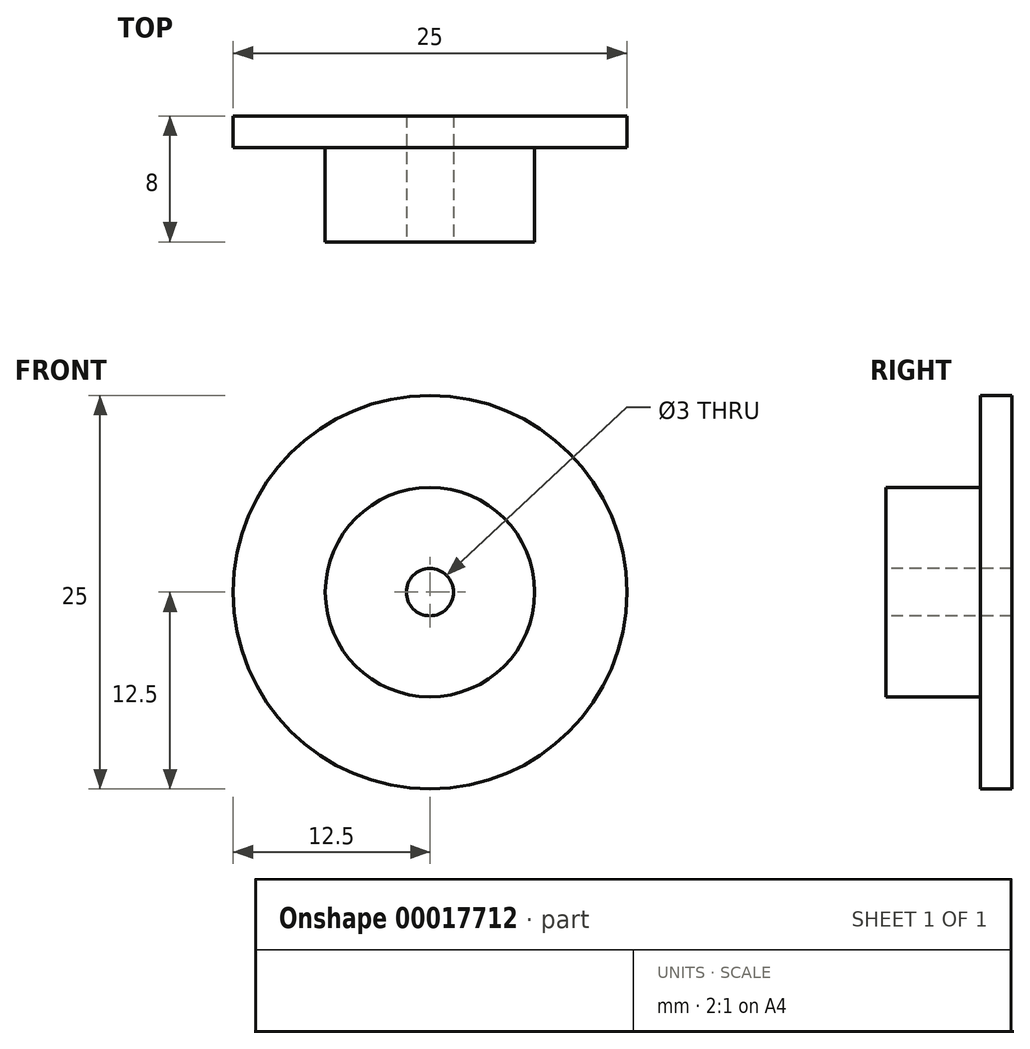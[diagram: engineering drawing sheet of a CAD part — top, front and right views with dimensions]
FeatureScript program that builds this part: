
annotation { "Feature Type Name" : "Feature", "Feature Type Description" : "" }
export const myFeature = defineFeature(function(context is Context, id is Id, definition is map)
    precondition{}
    {
        {
            var Q0;
            Q0=qCreatedBy(makeId("Front.planeOp"),FACE);
            var sketch = newSketch(context, id + "F0", { "sketchPlane" : qUnion([Q0])});
            skCircle(sketch, "E0", {"center": v(0, 0) * mm, "radius": 12.5 * mm});
            skSolve(sketch);
        }
        {
            var Q0;
            Q0 = qSketchRegion(id + "F0", true);
            extrude(context, id + "F1", {"entities" : qUnion([Q0]), "depth" : 2 * mm});
        }
        {
            var Q0;
            Q0=makeQuery(id+"F1.opExtrude","CAP_FACE",FACE,{"disambiguationData":[OSD([sQuery(id+"F0.wireOp",EDGE,"E0")])],"isStart":false});
            var sketch = newSketch(context, id + "F2", { "sketchPlane" : qUnion([Q0])});
            skCircle(sketch, "E1", {"center": v(0, 0) * mm, "radius": 6.65 * mm});
            skSolve(sketch);
        }
        {
            var Q0;
            Q0 = qSketchRegion(id + "F2", true);
            extrude(context, id + "F3", {"entities" : qUnion([Q0]), "operationType" : NewBodyOperationType.ADD, "depth" : 6 * mm});
        }
        {
            var Q0;
            Q0=makeQuery(id+"F3.opExtrude","CAP_FACE",FACE,{"disambiguationData":[OSD([sQuery(id+"F2.wireOp",EDGE,"E1")])],"isStart":false});
            var sketch = newSketch(context, id + "F4", { "sketchPlane" : qUnion([Q0])});
            skCircle(sketch, "E2", {"center": v(0, 0) * mm, "radius": 1.5 * mm});
            skSolve(sketch);
        }
        {
            var Q0;
            Q0 = qSketchRegion(id + "F4", true);
            extrude(context, id + "F5", {"entities" : qUnion([Q0]), "operationType" : NewBodyOperationType.REMOVE, "endBound" : BoundingType.THROUGH_ALL, "oppositeDirection" : true, "depth" : 25 * mm});
        }
    });
